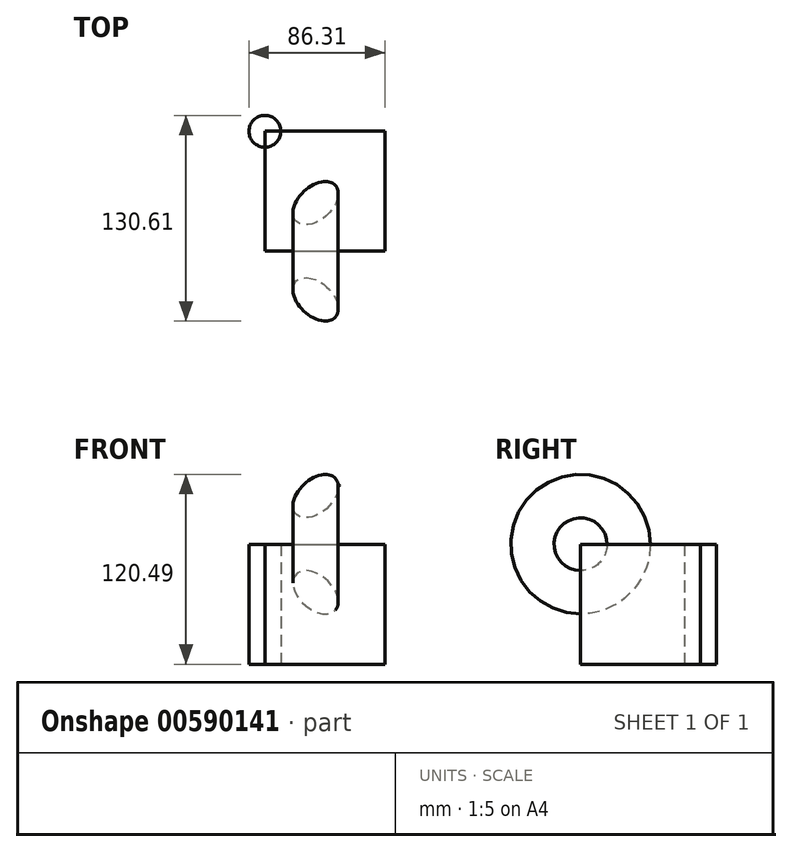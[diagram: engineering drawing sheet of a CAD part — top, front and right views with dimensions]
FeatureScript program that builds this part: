
annotation { "Feature Type Name" : "Feature", "Feature Type Description" : "" }
export const myFeature = defineFeature(function(context is Context, id is Id, definition is map)
    precondition{}
    {
        {
            var Q0;
            Q0=qCreatedBy(makeId("Top.planeOp"),FACE);
            var sketch = newSketch(context, id + "F0", { "sketchPlane" : qUnion([Q0])});
            skLineSegment(sketch, "E0.bottom", {"start": v(0, 0) * mm, "end": v(76.2, 0) * mm});
            skLineSegment(sketch, "E0.top", {"start": v(0, 76.2) * mm, "end": v(76.2, 76.2) * mm});
            skLineSegment(sketch, "E0.left", {"start": v(0, 0) * mm, "end": v(0, 76.2) * mm});
            skLineSegment(sketch, "E0.right", {"start": v(76.2, 0) * mm, "end": v(76.2, 76.2) * mm});
            skSolve(sketch);
        }
        {
            var Q0;
            Q0=makeQuery(id+"F0.imprint","IMPRINT",FACE,{"disambiguationData":[TD([[makeQuery(id+"F0.imprint","IMPRINT",EDGE,{"derivedFrom":sQuery(id+"F0.wireOp",EDGE,"E0.bottom")}),1.0]])]});
            var Q1;
            {var subQ0=sQuery(id+"F0.wireOp",EDGE,"E0.left");var subQ1=sQuery(id+"F0.wireOp",EDGE,"E0.top");var subQ2=makeQuery(id+"F0.imprint","INTERSECT",VERTEX,{"derivedFrom":[subQ1,subQ0]});Q1=makeQuery(id+"F0.imprint","IMPRINT",FACE,{"disambiguationData":[TD([[makeQuery(id+"F0.imprint","IMPRINT",EDGE,{"disambiguationData":[TD([[subQ2,-1.0]])],"derivedFrom":subQ1}),-1.0]])]});}
            extrude(context, id + "F1", {"entities" : qUnion([Q0, Q1]), "depth" : 76.2 * mm, "offsetDistance" : 25.4 * mm});
        }
        {
            var Q0;
            Q0=qCreatedBy(makeId("Front.planeOp"),FACE);
            var sketch = newSketch(context, id + "F2", { "sketchPlane" : qUnion([Q0])});
            skEllipse(sketch, "E1", {"center": v(32.22, 45.65) * mm, "majorRadius": 16.87 * mm, "minorRadius": 10.56 * mm, "majorAxis": v(0.74, -0.67)});
            skLineSegment(sketch, "E2", {"start": v(-21.09, 12.1) * mm, "end": v(-12.42, 3.82) * mm});
            skLineSegment(sketch, "E3", {"start": v(-12.42, 3.82) * mm, "end": v(-7.8, 8.65) * mm});
            skLineSegment(sketch, "E4", {"start": v(-21.09, 12.1) * mm, "end": v(-16.51, 16.88) * mm});
            skLineSegment(sketch, "E5", {"start": v(-16.51, 16.88) * mm, "end": v(-7.8, 8.65) * mm});
            skSolve(sketch);
        }
        {
            var Q0;
            Q0=makeQuery(id+"F2.imprint","IMPRINT",FACE,{"disambiguationData":[TD([[makeQuery(id+"F2.imprint","IMPRINT",EDGE,{"derivedFrom":sQuery(id+"F2.wireOp",EDGE,"E1")}),1.0]])]});
            var Q1;
            Q1=makeQuery(id+"F1.opExtrude","CAP_EDGE",EDGE,{"disambiguationData":[OSD([sQuery(id+"F0.wireOp",EDGE,"E0.bottom")])],"isStart":false});
            revolve(context, id + "F3", {"entities" : qUnion([Q0]), "axis" : qUnion([Q1]), "revolveType" : RevolveType.FULL});
        }
        {
            var Q0;
            Q0=qCreatedBy(makeId("Top.planeOp"),FACE);
            var sketch = newSketch(context, id + "F4", { "sketchPlane" : qUnion([Q0])});
            skCircle(sketch, "E6", {"center": v(0, 76.2) * mm, "radius": 10.1 * mm});
            skSolve(sketch);
        }
        {
            var Q0;
            Q0=makeQuery(id+"F4.imprint","IMPRINT",FACE,{"disambiguationData":[TD([[makeQuery(id+"F4.imprint","IMPRINT",EDGE,{"derivedFrom":sQuery(id+"F4.wireOp",EDGE,"E6")}),1.0]])]});
            var Q1;
            Q1=makeQuery(id+"F1.opExtrude","CAP_FACE",FACE,{"disambiguationData":[OSD([sQuery(id+"F0.wireOp",EDGE,"E0.bottom"),sQuery(id+"F0.wireOp",EDGE,"E0.top"),sQuery(id+"F0.wireOp",EDGE,"E0.left"),sQuery(id+"F0.wireOp",EDGE,"E0.right")])],"isStart":false});
            extrude(context, id + "F5", {"entities" : qUnion([Q0]), "endBound" : BoundingType.UP_TO_SURFACE, "depth" : 25.4 * mm, "endBoundEntityFace" : qUnion([Q1]), "offsetDistance" : 25.4 * mm});
        }
    });
